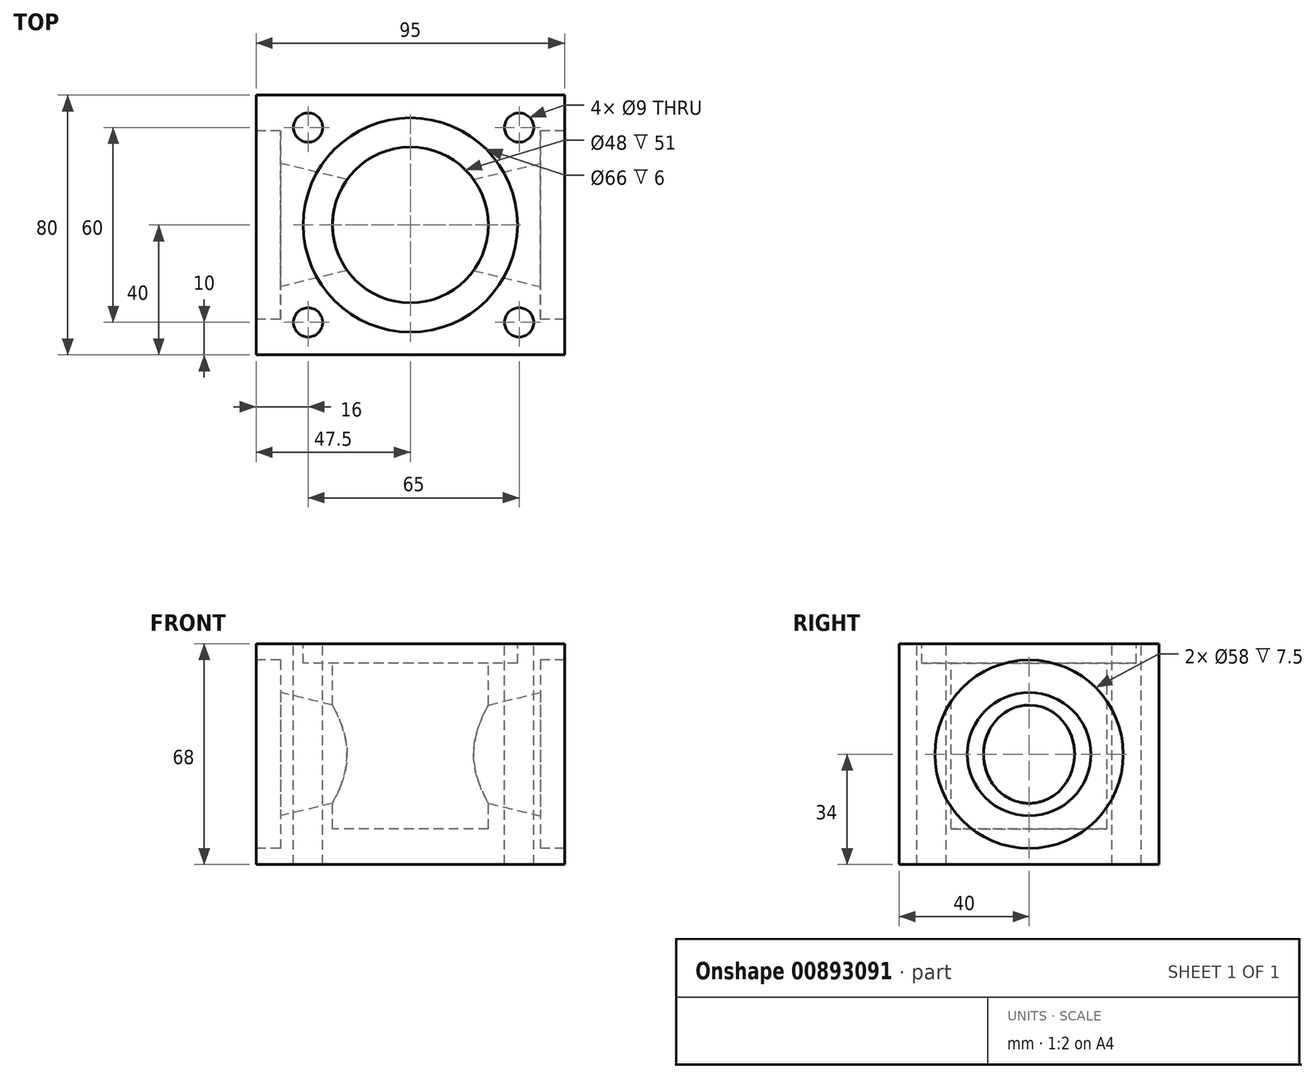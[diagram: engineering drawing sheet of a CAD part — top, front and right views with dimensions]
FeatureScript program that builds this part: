
annotation { "Feature Type Name" : "Feature", "Feature Type Description" : "" }
export const myFeature = defineFeature(function(context is Context, id is Id, definition is map)
    precondition{}
    {
        {
            var Q0;
            Q0=qCreatedBy(makeId("Top.planeOp"),FACE);
            var sketch = newSketch(context, id + "F0", { "sketchPlane" : qUnion([Q0])});
            skLineSegment(sketch, "E0.bottom", {"start": v(-47.5, 40) * mm, "end": v(47.5, 40) * mm});
            skLineSegment(sketch, "E0.top", {"start": v(-47.5, -40) * mm, "end": v(47.5, -40) * mm});
            skLineSegment(sketch, "E0.left", {"start": v(-47.5, 40) * mm, "end": v(-47.5, -40) * mm});
            skLineSegment(sketch, "E0.right", {"start": v(47.5, 40) * mm, "end": v(47.5, -40) * mm});
            skPoint(sketch, "E0.middle", {"position": v(0, 0) * mm});
            skSolve(sketch);
        }
        {
            var Q0;
            Q0=makeQuery(id+"F0.imprint","IMPRINT",FACE,{"disambiguationData":[TD([[makeQuery(id+"F0.imprint","IMPRINT",EDGE,{"derivedFrom":sQuery(id+"F0.wireOp",EDGE,"E0.bottom")}),-1.0]])]});
            extrude(context, id + "F1", {"entities" : qUnion([Q0]), "endBound" : BoundingType.SYMMETRIC, "depth" : 68 * mm, "offsetDistance" : 25 * mm});
        }
        {
            var Q0;
            Q0=qCreatedBy(makeId("Front.planeOp"),FACE);
            var sketch = newSketch(context, id + "F2", { "sketchPlane" : qUnion([Q0])});
            skLineSegment(sketch, "E1", {"start": v(0, 0) * mm, "end": v(47.5, 0) * mm, "construction": true});
            skLineSegment(sketch, "E2", {"start": v(47.5, 0) * mm, "end": v(47.5, 29) * mm, "construction": true});
            skLineSegment(sketch, "E3", {"start": v(47.5, 0) * mm, "end": v(47.5, -29) * mm, "construction": true});
            skLineSegment(sketch, "E4", {"start": v(47.5, 29) * mm, "end": v(40, 29) * mm});
            skLineSegment(sketch, "E5", {"start": v(40, 29) * mm, "end": v(40, 19) * mm});
            skLineSegment(sketch, "E6", {"start": v(47.5, 29) * mm, "end": v(47.5, -29) * mm});
            skLineSegment(sketch, "E7", {"start": v(47.5, -29) * mm, "end": v(40, -29) * mm});
            skLineSegment(sketch, "E8", {"start": v(40, -29) * mm, "end": v(40, -19) * mm});
            skLineSegment(sketch, "E9.MirrorCS", {"start": v(-47.5, -29) * mm, "end": v(-40, -29) * mm});
            skLineSegment(sketch, "E10.MirrorCS", {"start": v(-40, -29) * mm, "end": v(-40, -19) * mm});
            skLineSegment(sketch, "E11.MirrorCS", {"start": v(-47.5, 29) * mm, "end": v(-40, 29) * mm});
            skLineSegment(sketch, "E12.MirrorCS", {"start": v(-40, 29) * mm, "end": v(-40, 19) * mm});
            skLineSegment(sketch, "E13", {"start": v(-47.5, 29) * mm, "end": v(-47.5, -29) * mm});
            skLineSegment(sketch, "E14", {"start": v(-60.77, 0) * mm, "end": v(59.85, 0) * mm, "construction": true});
            skLineSegment(sketch, "E15", {"start": v(-47.5, 0) * mm, "end": v(47.5, 0) * mm});
            skLineSegment(sketch, "E16", {"start": v(40, 19) * mm, "end": v(40, -19) * mm, "construction": true});
            skLineSegment(sketch, "E17", {"start": v(-40, 19) * mm, "end": v(-40, -19) * mm, "construction": true});
            skLineSegment(sketch, "E18", {"start": v(-40, 0) * mm, "end": v(-10, 0) * mm, "construction": true});
            skLineSegment(sketch, "E19", {"start": v(40, 0) * mm, "end": v(10, 0) * mm, "construction": true});
            skLineSegment(sketch, "E20", {"start": v(10, 11.73) * mm, "end": v(10, -11.73) * mm, "construction": true});
            skLineSegment(sketch, "E21", {"start": v(-10, 11.73) * mm, "end": v(-10, -11.73) * mm, "construction": true});
            skLineSegment(sketch, "E22", {"start": v(-40, 19) * mm, "end": v(-10, 11.73) * mm});
            skLineSegment(sketch, "E23", {"start": v(-10, 11.73) * mm, "end": v(10, 11.73) * mm});
            skLineSegment(sketch, "E24", {"start": v(10, 11.73) * mm, "end": v(40, 19) * mm});
            skLineSegment(sketch, "E25", {"start": v(40, -19) * mm, "end": v(10, -11.73) * mm});
            skLineSegment(sketch, "E26", {"start": v(10, -11.73) * mm, "end": v(-10, -11.73) * mm});
            skLineSegment(sketch, "E27", {"start": v(-10, -11.73) * mm, "end": v(-40, -19) * mm});
            skSolve(sketch);
        }
        {
            var Q0;
            {var subQ1=sQuery(id+"F2.wireOp",EDGE,"E4");Q0=makeQuery(id+"F2.imprint","IMPRINT",FACE,{"disambiguationData":[TD([[makeQuery(id+"F2.imprint","IMPRINT",EDGE,{"derivedFrom":subQ1}),1.0]])]});}
            var Q1;
            Q1=sQuery(id+"F2.wireOp",EDGE,"E14");
            revolve(context, id + "F3", {"operationType" : NewBodyOperationType.REMOVE, "surfaceOperationType" : NewSurfaceOperationType.NEW, "entities" : qUnion([Q0]), "axis" : qUnion([Q1]), "revolveType" : RevolveType.FULL});
        }
        {
            var Q0;
            Q0=makeQuery(id+"F1.opExtrude","CAP_FACE",FACE,{"disambiguationData":[OSD([sQuery(id+"F0.wireOp",EDGE,"E0.bottom"),sQuery(id+"F0.wireOp",EDGE,"E0.top"),sQuery(id+"F0.wireOp",EDGE,"E0.left"),sQuery(id+"F0.wireOp",EDGE,"E0.right")])],"isStart":false});
            var sketch = newSketch(context, id + "F4", { "sketchPlane" : qUnion([Q0])});
            skCircle(sketch, "E28", {"center": v(0, 0) * mm, "radius": 33 * mm});
            skCircle(sketch, "E29", {"center": v(0, 0) * mm, "radius": 24 * mm});
            skLineSegment(sketch, "E30.bottom", {"start": v(-47.5, 40) * mm, "end": v(47.5, 40) * mm, "construction": true});
            skLineSegment(sketch, "E30.top", {"start": v(-47.5, -40) * mm, "end": v(47.5, -40) * mm, "construction": true});
            skLineSegment(sketch, "E30.left", {"start": v(-47.5, 40) * mm, "end": v(-47.5, -40) * mm, "construction": true});
            skLineSegment(sketch, "E30.right", {"start": v(47.5, 40) * mm, "end": v(47.5, -40) * mm, "construction": true});
            skLineSegment(sketch, "E31", {"start": v(-47.5, 40) * mm, "end": v(-31.5, 40) * mm, "construction": true});
            skLineSegment(sketch, "E32", {"start": v(-31.5, 40) * mm, "end": v(-31.5, -40) * mm, "construction": true});
            skLineSegment(sketch, "E33", {"start": v(47.5, 40) * mm, "end": v(33.5, 40) * mm, "construction": true});
            skLineSegment(sketch, "E34", {"start": v(33.5, 40) * mm, "end": v(33.5, -40) * mm, "construction": true});
            skLineSegment(sketch, "E35", {"start": v(47.5, 40) * mm, "end": v(47.5, 30) * mm, "construction": true});
            skLineSegment(sketch, "E36", {"start": v(47.5, -40) * mm, "end": v(47.5, -30) * mm, "construction": true});
            skLineSegment(sketch, "E37", {"start": v(47.5, -30) * mm, "end": v(-47.5, -30) * mm, "construction": true});
            skLineSegment(sketch, "E38", {"start": v(47.5, 30) * mm, "end": v(-47.5, 30) * mm, "construction": true});
            skCircle(sketch, "E39", {"center": v(-31.5, 30) * mm, "radius": 4.5 * mm});
            skCircle(sketch, "E40", {"center": v(33.5, 30) * mm, "radius": 4.5 * mm});
            skCircle(sketch, "E41", {"center": v(-31.5, -30) * mm, "radius": 4.5 * mm});
            skCircle(sketch, "E42", {"center": v(33.5, -30) * mm, "radius": 4.5 * mm});
            skSolve(sketch);
        }
        {
            var Q0;
            Q0=makeQuery(id+"F4.imprint","IMPRINT",FACE,{"disambiguationData":[TD([[makeQuery(id+"F4.imprint","IMPRINT",EDGE,{"derivedFrom":sQuery(id+"F4.wireOp",EDGE,"E39")}),1.0]])]});
            var Q1;
            Q1=makeQuery(id+"F4.imprint","IMPRINT",FACE,{"disambiguationData":[TD([[makeQuery(id+"F4.imprint","IMPRINT",EDGE,{"derivedFrom":sQuery(id+"F4.wireOp",EDGE,"E40")}),1.0]])]});
            var Q2;
            Q2=makeQuery(id+"F4.imprint","IMPRINT",FACE,{"disambiguationData":[TD([[makeQuery(id+"F4.imprint","IMPRINT",EDGE,{"derivedFrom":sQuery(id+"F4.wireOp",EDGE,"E41")}),1.0]])]});
            var Q3;
            Q3=makeQuery(id+"F4.imprint","IMPRINT",FACE,{"disambiguationData":[TD([[makeQuery(id+"F4.imprint","IMPRINT",EDGE,{"derivedFrom":sQuery(id+"F4.wireOp",EDGE,"E42")}),1.0]])]});
            extrude(context, id + "F5", {"entities" : qUnion([Q0, Q1, Q2, Q3]), "operationType" : NewBodyOperationType.REMOVE, "oppositeDirection" : true, "depth" : 68 * mm, "offsetDistance" : 25 * mm});
        }
        {
            var Q0;
            Q0=makeQuery(id+"F4.imprint","IMPRINT",FACE,{"disambiguationData":[TD([[makeQuery(id+"F4.imprint","IMPRINT",EDGE,{"derivedFrom":sQuery(id+"F4.wireOp",EDGE,"E29")}),1.0]])]});
            extrude(context, id + "F6", {"entities" : qUnion([Q0]), "operationType" : NewBodyOperationType.REMOVE, "oppositeDirection" : true, "depth" : 57 * mm, "offsetDistance" : 25 * mm});
        }
        {
            var Q0;
            Q0=makeQuery(id+"F4.imprint","IMPRINT",FACE,{"disambiguationData":[TD([[makeQuery(id+"F4.imprint","IMPRINT",EDGE,{"derivedFrom":sQuery(id+"F4.wireOp",EDGE,"E28")}),1.0]])]});
            extrude(context, id + "F7", {"entities" : qUnion([Q0]), "operationType" : NewBodyOperationType.REMOVE, "oppositeDirection" : true, "depth" : 6 * mm, "offsetDistance" : 25 * mm});
        }
    });
